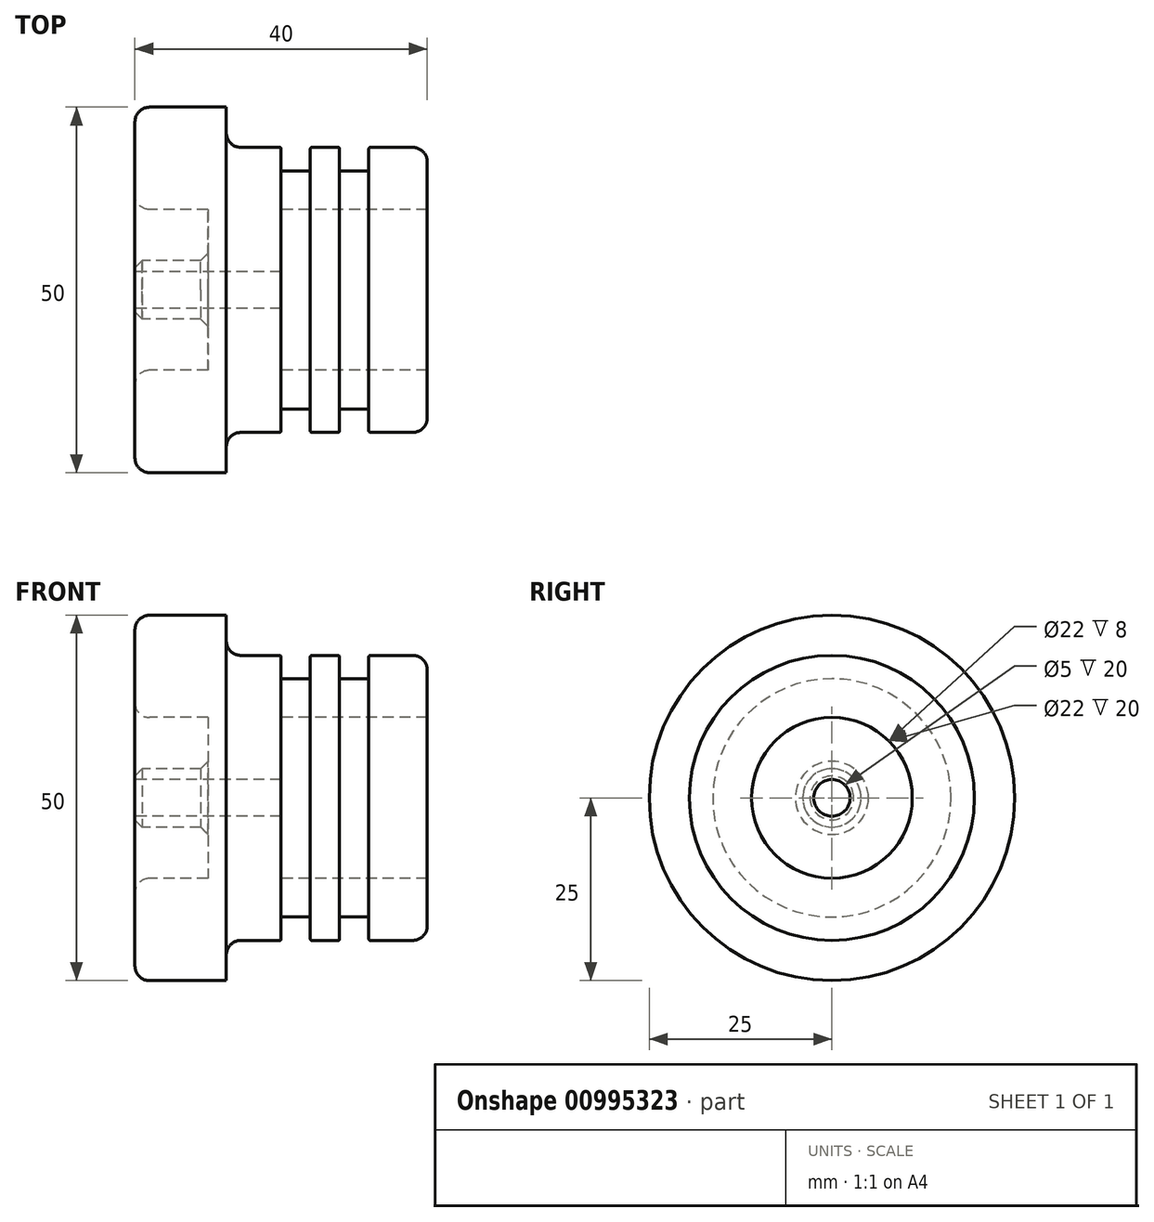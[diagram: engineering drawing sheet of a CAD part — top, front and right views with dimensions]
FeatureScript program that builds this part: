
annotation { "Feature Type Name" : "Feature", "Feature Type Description" : "" }
export const myFeature = defineFeature(function(context is Context, id is Id, definition is map)
    precondition{}
    {
        {
            var Q0;
            Q0=qCreatedBy(makeId("Front.planeOp"),FACE);
            var sketch = newSketch(context, id + "F0", { "sketchPlane" : qUnion([Q0])});
            skLineSegment(sketch, "E0", {"start": v(-20, 2.5) * mm, "end": v(-20, 4) * mm});
            skLineSegment(sketch, "E1", {"start": v(-20, 25) * mm, "end": v(-7.5, 25) * mm});
            skLineSegment(sketch, "E2", {"start": v(-7.5, 25) * mm, "end": v(-7.5, 19.5) * mm});
            skLineSegment(sketch, "E3", {"start": v(-7.5, 19.5) * mm, "end": v(0, 19.5) * mm});
            skLineSegment(sketch, "E4", {"start": v(0, 19.5) * mm, "end": v(0, 16.3) * mm});
            skLineSegment(sketch, "E5", {"start": v(0, 16.3) * mm, "end": v(4, 16.3) * mm});
            skLineSegment(sketch, "E6", {"start": v(4, 16.3) * mm, "end": v(4, 19.5) * mm});
            skLineSegment(sketch, "E7", {"start": v(4, 19.5) * mm, "end": v(8, 19.5) * mm});
            skLineSegment(sketch, "E8", {"start": v(20, 19.5) * mm, "end": v(20, 11) * mm});
            skCircle(sketch, "E9", {"center": v(2.19, 18.1) * mm, "radius": 1.8 * mm});
            skLineSegment(sketch, "E10", {"start": v(-20, 11) * mm, "end": v(-10, 11) * mm});
            skLineSegment(sketch, "E11", {"start": v(-10, 11) * mm, "end": v(-10, 4) * mm});
            skLineSegment(sketch, "E12", {"start": v(-10, 4) * mm, "end": v(-20, 4) * mm});
            skLineSegment(sketch, "E13", {"start": v(-20, 4) * mm, "end": v(-20, 2.5) * mm});
            skLineSegment(sketch, "E14", {"start": v(-20, 2.5) * mm, "end": v(0, 2.5) * mm});
            skLineSegment(sketch, "E15", {"start": v(0, 2.5) * mm, "end": v(0, 11) * mm});
            skLineSegment(sketch, "E16", {"start": v(0, 11) * mm, "end": v(20, 11) * mm});
            skLineSegment(sketch, "E17.trimOffspring", {"start": v(-20, 11) * mm, "end": v(-20, 25) * mm});
            skLineSegment(sketch, "E18", {"start": v(-14.17, 0) * mm, "end": v(11.3, 0) * mm, "construction": true});
            skLineSegment(sketch, "E19", {"start": v(8, 19.5) * mm, "end": v(8, 16.3) * mm});
            skLineSegment(sketch, "E20", {"start": v(8, 16.3) * mm, "end": v(12, 16.3) * mm});
            skLineSegment(sketch, "E21", {"start": v(12, 16.3) * mm, "end": v(12, 19.5) * mm});
            skLineSegment(sketch, "E22.trimOffspring", {"start": v(12, 19.5) * mm, "end": v(20, 19.5) * mm});
            skSolve(sketch);
        }
        {
            var Q0;
            Q0=makeQuery(id+"F0.imprint","IMPRINT",FACE,{"disambiguationData":[TD([[makeQuery(id+"F0.imprint","IMPRINT",EDGE,{"derivedFrom":sQuery(id+"F0.wireOp",EDGE,"E1")}),-1.0]])]});
            var Q1;
            Q1=sQuery(id+"F0.wireOp",EDGE,"E18");
            var Q2;
            Q2=sQuery(id+"F0.wireOp",EDGE,"E18");
            revolve(context, id + "F1", {"surfaceOperationType" : NewSurfaceOperationType.NEW, "entities" : qUnion([Q0]), "surfaceEntities" : qUnion([Q1]), "axis" : qUnion([Q2]), "revolveType" : RevolveType.FULL});
        }
        {
            var Q0;
            Q0=makeQuery(id+"F1.opRevolve","SWEPT_EDGE",EDGE,{"disambiguationData":[OSD([sQuery(id+"F0.wireOp",EDGE,"E1"),sQuery(id+"F0.wireOp",EDGE,"E17.trimOffspring")])]});
            var Q1;
            Q1=makeQuery(id+"F1.opRevolve","SWEPT_EDGE",EDGE,{"disambiguationData":[OSD([sQuery(id+"F0.wireOp",EDGE,"E10"),sQuery(id+"F0.wireOp",EDGE,"E17.trimOffspring")])]});
            var Q2;
            Q2=makeQuery(id+"F1.opRevolve","SWEPT_EDGE",EDGE,{"disambiguationData":[OSD([sQuery(id+"F0.wireOp",EDGE,"E8"),sQuery(id+"F0.wireOp",EDGE,"E22.trimOffspring")])]});
            var Q3;
            Q3=makeQuery(id+"F1.opRevolve","SWEPT_EDGE",EDGE,{"disambiguationData":[OSD([sQuery(id+"F0.wireOp",EDGE,"E2"),sQuery(id+"F0.wireOp",EDGE,"E3")])]});
            var Q4;
            Q4=makeQuery(id+"FLEeYUfBkV8Y8wr_1.boolean.opBoolean","COPY",EDGE,{"derivedFrom":makeQuery(id+"FLEeYUfBkV8Y8wr_1.opExtrude","SWEPT_EDGE",EDGE,{"disambiguationData":[OSD([sQuery(id+"FNQseuMmu8bz8QX_1.wireOp",EDGE,"513d5dc0-d951-4f4c-8608-e21d25f3eba40.MirrorCS"),sQuery(id+"FNQseuMmu8bz8QX_1.wireOp",EDGE,"ce85addf-061e-4623-82e5-87099950fa100.MirrorCS")])]})});
            var Q5;
            Q5=makeQuery(id+"FLEeYUfBkV8Y8wr_1.boolean.opBoolean","COPY",EDGE,{"derivedFrom":makeQuery(id+"FLEeYUfBkV8Y8wr_1.opExtrude","SWEPT_EDGE",EDGE,{"disambiguationData":[OSD([sQuery(id+"FNQseuMmu8bz8QX_1.wireOp",EDGE,"n7cqBilH-qRB2-xxOZ-w1iX-4wN83PTupIgn.top"),sQuery(id+"FNQseuMmu8bz8QX_1.wireOp",EDGE,"n7cqBilH-qRB2-xxOZ-w1iX-4wN83PTupIgn.right")])]})});
            var Q6;
            Q6=makeQuery(id+"FLEeYUfBkV8Y8wr_1.boolean.opBoolean","INTERSECT",EDGE,{"derivedFrom":[makeQuery(id+"F1.opRevolve","SWEPT_FACE",FACE,{"disambiguationData":[OSD([sQuery(id+"F0.wireOp",EDGE,"E1")])]}),makeQuery(id+"FLEeYUfBkV8Y8wr_1.opExtrude","SWEPT_FACE",FACE,{"disambiguationData":[OSD([sQuery(id+"FNQseuMmu8bz8QX_1.wireOp",EDGE,"n7cqBilH-qRB2-xxOZ-w1iX-4wN83PTupIgn.left")])]})]});
            var Q7;
            Q7=makeQuery(id+"FLEeYUfBkV8Y8wr_1.boolean.opBoolean","INTERSECT",EDGE,{"derivedFrom":[makeQuery(id+"F1.opRevolve","SWEPT_FACE",FACE,{"disambiguationData":[OSD([sQuery(id+"F0.wireOp",EDGE,"E1")])]}),makeQuery(id+"FLEeYUfBkV8Y8wr_1.opExtrude","SWEPT_FACE",FACE,{"disambiguationData":[OSD([sQuery(id+"FNQseuMmu8bz8QX_1.wireOp",EDGE,"1e4829f3-3866-439c-9bfe-a7541cfa9a150.MirrorCS")])]})]});
            fillet(context, id + "F2", {"entities" : qUnion([Q0, Q1, Q2, Q3, Q4, Q5, Q6, Q7]), "radius" : 2 * mm, "tangentPropagation" : true, "allowEdgeOverflow" : false});
        }
        {
            var Q0;
            Q0=makeQuery(id+"F1.opRevolve","SWEPT_EDGE",EDGE,{"disambiguationData":[OSD([sQuery(id+"F0.wireOp",EDGE,"E12"),sQuery(id+"F0.wireOp",EDGE,"E13")])]});
            chamfer(context, id + "F3", {"entities" : qUnion([Q0]), "width" : 1 * mm, "tangentPropagation" : true});
        }
        {
            var Q0;
            Q0=makeQuery(id+"F1.opRevolve","SWEPT_EDGE",EDGE,{"disambiguationData":[OSD([sQuery(id+"F0.wireOp",EDGE,"E3"),sQuery(id+"F0.wireOp",EDGE,"E4")])]});
            var Q1;
            Q1=makeQuery(id+"F1.opRevolve","SWEPT_EDGE",EDGE,{"disambiguationData":[OSD([sQuery(id+"F0.wireOp",EDGE,"E6"),sQuery(id+"F0.wireOp",EDGE,"E7")])]});
            var Q2;
            Q2=makeQuery(id+"F1.opRevolve","SWEPT_EDGE",EDGE,{"disambiguationData":[OSD([sQuery(id+"F0.wireOp",EDGE,"E7"),sQuery(id+"F0.wireOp",EDGE,"E19")])]});
            var Q3;
            Q3=makeQuery(id+"F1.opRevolve","SWEPT_EDGE",EDGE,{"disambiguationData":[OSD([sQuery(id+"F0.wireOp",EDGE,"E21"),sQuery(id+"F0.wireOp",EDGE,"E22.trimOffspring")])]});
            fillet(context, id + "F4", {"entities" : qUnion([Q0, Q1, Q2, Q3]), "radius" : 0.2 * mm, "tangentPropagation" : true, "allowEdgeOverflow" : false});
        }
    });
